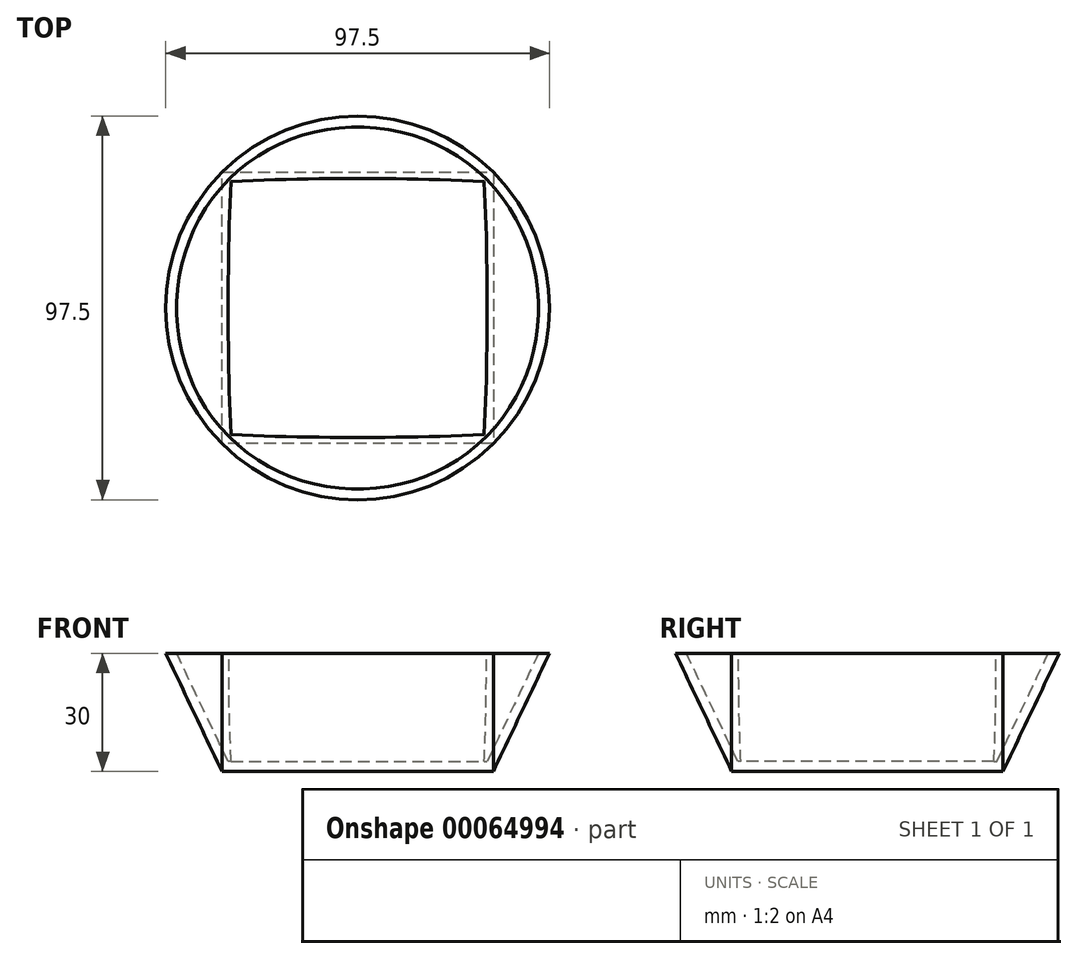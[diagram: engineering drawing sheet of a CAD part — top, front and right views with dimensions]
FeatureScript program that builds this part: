
annotation { "Feature Type Name" : "Feature", "Feature Type Description" : "" }
export const myFeature = defineFeature(function(context is Context, id is Id, definition is map)
    precondition{}
    {
        {
            var Q0;
            Q0=qCreatedBy(makeId("Top.planeOp"),FACE);
            var sketch = newSketch(context, id + "F0", { "sketchPlane" : qUnion([Q0])});
            skCircle(sketch, "E0", {"center": v(0, 0) * mm, "radius": 48.75 * mm});
            skSolve(sketch);
        }
        {
            var Q0;
            Q0=qCreatedBy(makeId("Top.planeOp"),FACE);
            cPlane(context, id + "F1", {"entities" : qUnion([Q0]), "cplaneType" : CPlaneType.OFFSET, "offset" : 30 * mm, "oppositeDirection" : true, "width" : 150 * mm, "height" : 150 * mm});
        }
        {
            var Q0;
            Q0=qCreatedBy(id+"F1.planeOp",FACE);
            var sketch = newSketch(context, id + "F2", { "sketchPlane" : qUnion([Q0])});
            skCircle(sketch, "E1.cCircle", {"center": v(0, 0) * mm, "radius": 34.47 * mm, "construction": true});
            skLineSegment(sketch, "E1.0", {"start": v(34.47, -34.47) * mm, "end": v(-34.47, -34.47) * mm});
            skLineSegment(sketch, "E1.1", {"start": v(-34.47, -34.47) * mm, "end": v(-34.47, 34.47) * mm});
            skLineSegment(sketch, "E1.2", {"start": v(-34.47, 34.47) * mm, "end": v(34.47, 34.47) * mm});
            skLineSegment(sketch, "E1.3", {"start": v(34.47, 34.47) * mm, "end": v(34.47, -34.47) * mm});
            skPoint(sketch, "E1.0.midPoint", {"position": v(0, -34.47) * mm});
            skSolve(sketch);
        }
        {
            var Q0;
            Q0=makeQuery(id+"F0.imprint","IMPRINT",FACE,{"disambiguationData":[TD([[makeQuery(id+"F0.imprint","IMPRINT",EDGE,{"derivedFrom":sQuery(id+"F0.wireOp",EDGE,"E0")}),1.0]])]});
            var Q1;
            Q1=makeQuery(id+"F2.imprint","IMPRINT",FACE,{"disambiguationData":[TD([[makeQuery(id+"F2.imprint","IMPRINT",EDGE,{"derivedFrom":sQuery(id+"F2.wireOp",EDGE,"E1.0")}),-1.0]])]});
            loft(context, id + "F3", {"sheetProfilesArray" : [{ "sheetProfileEntities" : qUnion([Q0]) }, { "sheetProfileEntities" : qUnion([Q1]) }]});
        }
        {
            var Q0;
            Q0=makeQuery(id+"F3.opLoft","CAP_FACE",FACE,{"disambiguationData":[OSD([makeQuery(id+"F0.imprint","IMPRINT",FACE,{"disambiguationData":[TD([[makeQuery(id+"F0.imprint","IMPRINT",EDGE,{"derivedFrom":sQuery(id+"F0.wireOp",EDGE,"E0")}),1.0]])]})])],"isStart":true});
            shell(context, id + "F4", {"entities" : qUnion([Q0]), "thickness" : 2.5 * mm});
        }
    });
